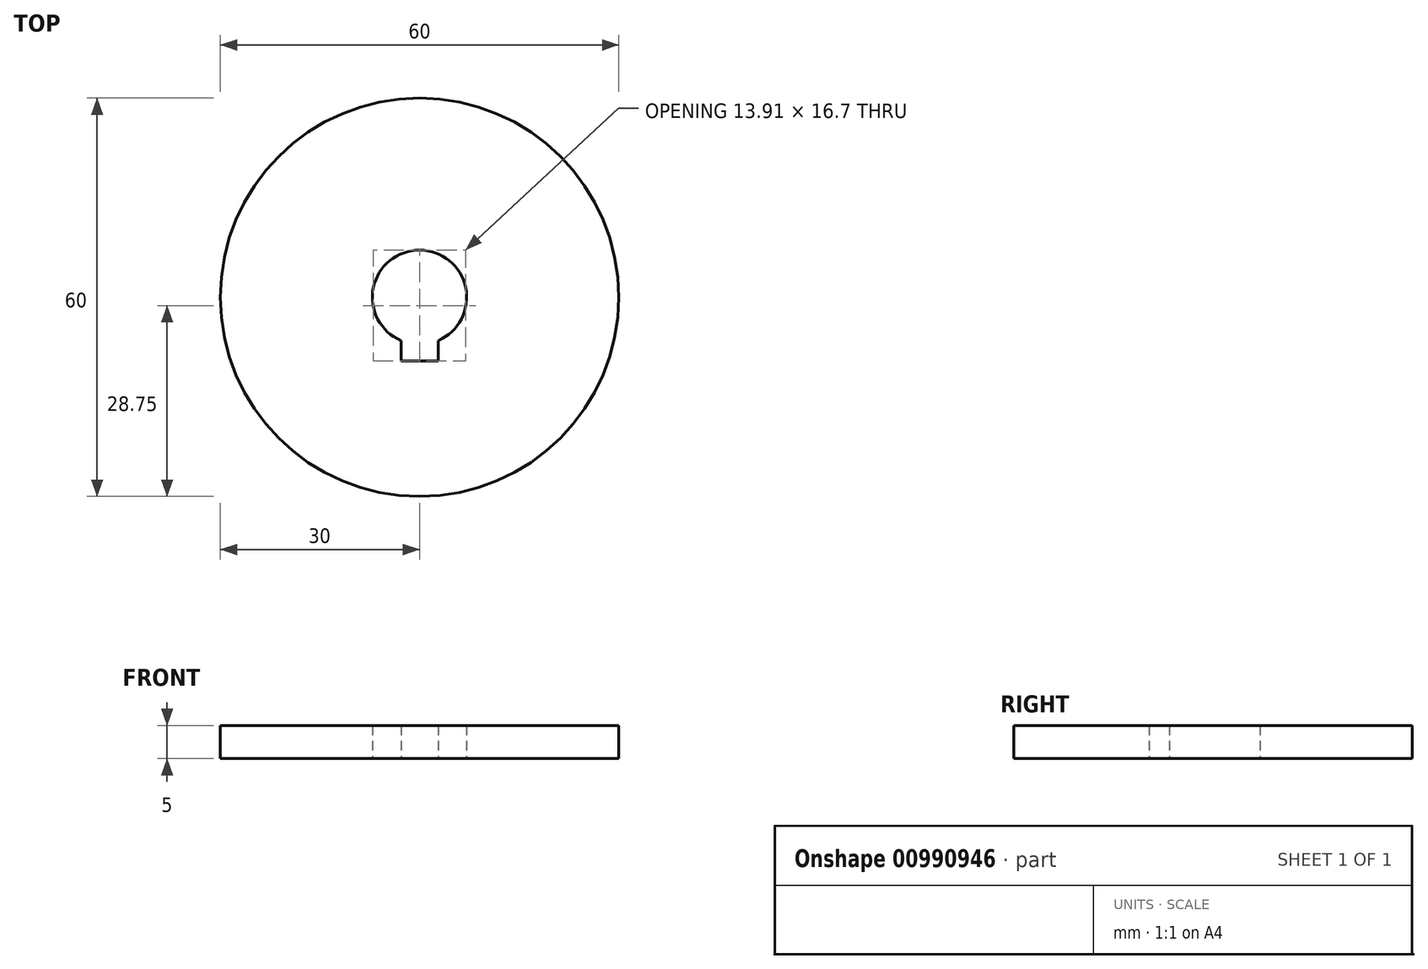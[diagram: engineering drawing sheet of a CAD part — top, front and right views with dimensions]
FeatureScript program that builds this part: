
annotation { "Feature Type Name" : "Feature", "Feature Type Description" : "" }
export const myFeature = defineFeature(function(context is Context, id is Id, definition is map)
    precondition{}
    {
        {
            var Q0;
            Q0=qCreatedBy(makeId("Top.planeOp"),FACE);
            var sketch = newSketch(context, id + "F0", { "sketchPlane" : qUnion([Q0])});
            skCircle(sketch, "E0", {"center": v(0, 0) * mm, "radius": 7.1 * mm});
            skLineSegment(sketch, "E1", {"start": v(0, 0) * mm, "end": v(0, -9.6) * mm, "construction": true});
            skLineSegment(sketch, "E2", {"start": v(0, -9.6) * mm, "end": v(-2.8, -9.6) * mm});
            skLineSegment(sketch, "E3", {"start": v(-2.8, -9.6) * mm, "end": v(-2.8, -6.52) * mm});
            skCircle(sketch, "E4", {"center": v(0, 0) * mm, "radius": 30 * mm});
            skPoint(sketch, "E5", {"position": v(0, -7.1) * mm});
            skLineSegment(sketch, "E6.MirrorCS", {"start": v(0, -9.6) * mm, "end": v(2.8, -9.6) * mm});
            skLineSegment(sketch, "E7.MirrorCS", {"start": v(2.8, -9.6) * mm, "end": v(2.8, -6.52) * mm});
            skSolve(sketch);
        }
        {
            var Q0;
            Q0=makeQuery(id+"F0.imprint","IMPRINT",FACE,{"disambiguationData":[TD([[makeQuery(id+"F0.imprint","IMPRINT",EDGE,{"derivedFrom":sQuery(id+"F0.wireOp",EDGE,"E2")}),1.0]])]});
            extrude(context, id + "F1", {"entities" : qUnion([Q0]), "endBound" : BoundingType.SYMMETRIC, "depth" : 5 * mm, "offsetDistance" : 25 * mm});
        }
    });
